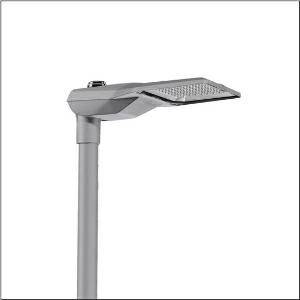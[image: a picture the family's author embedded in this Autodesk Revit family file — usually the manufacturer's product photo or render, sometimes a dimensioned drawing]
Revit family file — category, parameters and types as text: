
# Revit family: streetlight_sl_21_midi___st1_0a_5xe7d47n08lb_f0d9
name_source: partatom
category: Lighting Fixtures
units: mm (PartAtom-declared; Revit-internal decimal feet)

## family parameters
Cut with Voids When Loaded = No
Host = Face
Light Source = No
Part Type = Normal
Room Calculation Point = No
Round Connector Dimension = Use Diameter
Shared = No

## types (1)
- --- (1 x LED, 14950 lm, 98.3 W, 4000K)
    Apparent Load = 98 VA
    CIE Flux Codes = 37 72 97 100 100
    Color Rendering = 70
    Color Temperature = 4000K
    Default Elevation = 1800 mm
    Description = Streetlight SL 21 midi, mast luminaire, primary light control with lens, of PMMA, primary optical cover: cover, of toughened safety glass, transparent, light distribution: ST1.0a, light emission: direct distribution, primary light characteristic: asymmetric, installation type: side-entry, LED, 3G 2.5mm², High Power LED, rated luminous flux: 14.950lm, luminous efficacy: 152lm/W, light colour: 740, colour temperature: 4000K, control: overheat protection, presetting dimming linear, constant luminous flux control, time-dependent luminous flux control, flexible luminous flux parameterisation, mains connection: 220..240V, AC, 50/60Hz, connection cable pre-assembled, cable length: 10,5m, wiring characteristics: H05VV-F, start of lifetime: 98W, end of service life: 101W, reduction: 45W, luminaire housing, of diecast aluminium (EN AC-44300), powder-coated, Siteco® metallic grey (DB 702S), corrosivity category C5 mid according to DIN EN ISO 12944, multi-level sealing system, sealing non-destructively replaceable, inclination adjustable: 0°, 5°, 10°, 15°, length: 644mm, width: 335mm, height: 110mm, spigot size: 42mm (side-entry), protection rating (complete): IP66, insulation class (complete): insulation class I (protective earthing), certification: CE, ENEC, ENEC+, VDE, impact resistance: IK09, permissible operating ambient temperature for outdoor applications: -40..+50°C, standard-compliant lighting for roads and squares, packaging unit: 1 piece

Light Distribution: ST1.0a
    Height = 111 mm
    Lamp = 1 x LED
    Lamp Light Flux = 14950 lm
    Lamp Power = 98.3 W
    Lamp count = 1
    Length = 644 mm
    Luminous efficacy = 152 lm/W
    Manufacturer = Siteco
    ModVariant = No
    Model = 5XE7D47N08LB
    Number of Poles = 1
    OnlyDefault = Yes
    Power Factor = 1
    Product Name = Streetlight SL 21 midi | ST1.0a
    Product group = mast luminaire | pylon top
    ProductGroupID = 6100
    Protection Class = Protection class I
    Protection Degree = IP 66
    RLX_Detail_Level = 1
    RLX_Emergency_Light_Flux = 0 lm
    RLX_Emergency_Type = 0
    RLX_Emergency_Type_DB = No
    RlxData = <blob elided: 90565 chars, md5=fab33d54>
    Socket = socket
    Standby Power = 0 W
    System Light Flux = 14950 lm
    System Power = 98 W
    Type Comments = factory setting: luminous flux: 100 % | dim-lin: 254 | 1020 mA
    Type Image = l_1294377.jpg
    URL = http://relux.com
    VarID = @adj_085385
    Voltage = 0 V
    Weight = 0.00 kg
    Width = 336 mm

## geometry (parser evidence)
native form markers: Blend x4, Sweep x10
no freeform markers — native parametric forms only
